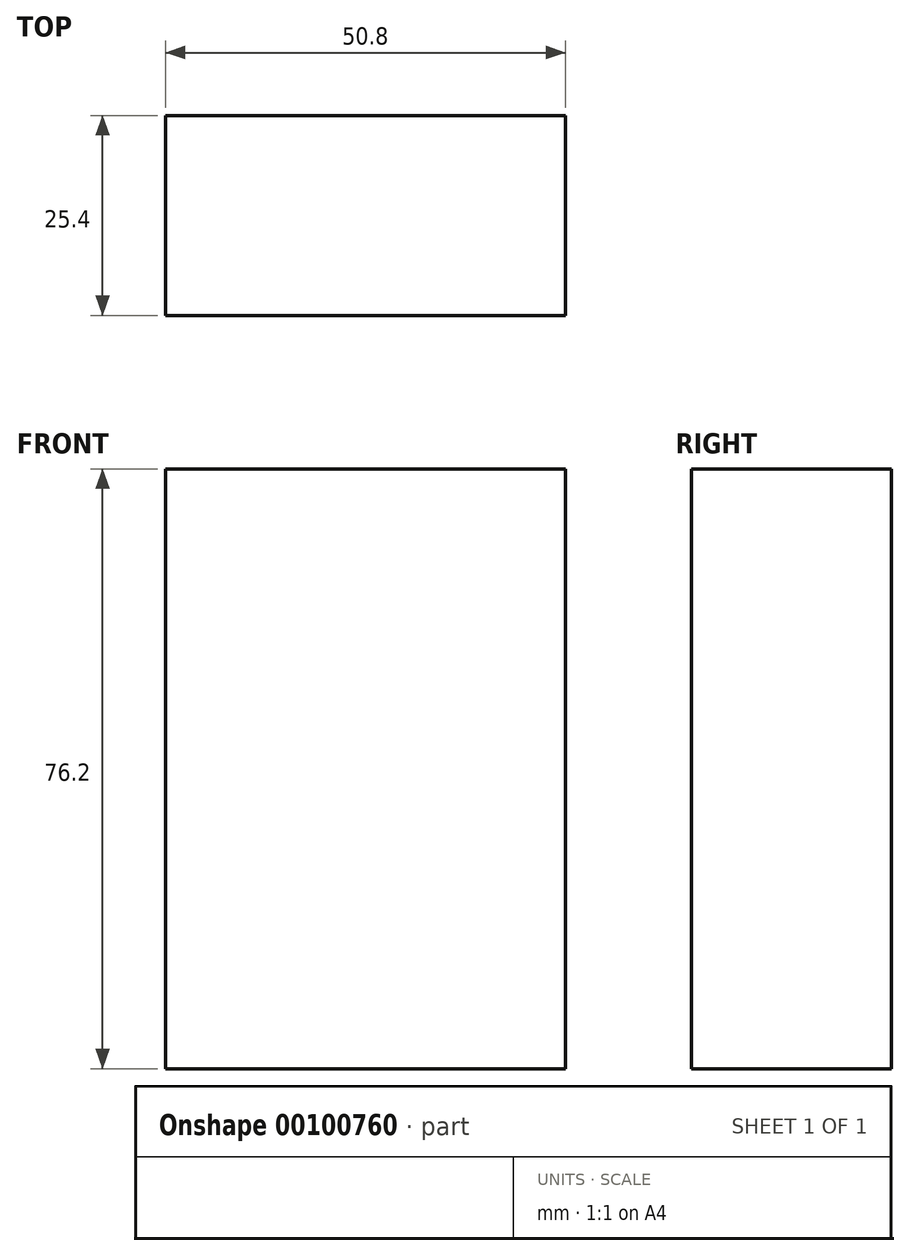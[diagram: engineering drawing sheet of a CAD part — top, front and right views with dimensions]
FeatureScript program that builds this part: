
annotation { "Feature Type Name" : "Feature", "Feature Type Description" : "" }
export const myFeature = defineFeature(function(context is Context, id is Id, definition is map)
    precondition{}
    {
        {
            var Q0;
            Q0=qCreatedBy(makeId("Front.planeOp"),FACE);
            var sketch = newSketch(context, id + "F0", { "sketchPlane" : qUnion([Q0])});
            skLineSegment(sketch, "E0.bottom", {"start": v(-25.4, 38.1) * mm, "end": v(25.4, 38.1) * mm});
            skLineSegment(sketch, "E0.top", {"start": v(-25.4, -38.1) * mm, "end": v(25.4, -38.1) * mm});
            skLineSegment(sketch, "E0.left", {"start": v(-25.4, 38.1) * mm, "end": v(-25.4, -38.1) * mm});
            skLineSegment(sketch, "E0.right", {"start": v(25.4, 38.1) * mm, "end": v(25.4, -38.1) * mm});
            skPoint(sketch, "E0.middle", {"position": v(0, 0) * mm});
            skSolve(sketch);
        }
        {
            var Q0;
            Q0=makeQuery(id+"F0.imprint","IMPRINT",FACE,{"disambiguationData":[TD([[makeQuery(id+"F0.imprint","IMPRINT",EDGE,{"derivedFrom":sQuery(id+"F0.wireOp",EDGE,"E0.bottom")}),-1.0]])]});
            extrude(context, id + "F1", {"entities" : qUnion([Q0]), "depth" : 25.4 * mm});
        }
        {
            var Q0;
            Q0 = qSketchRegion(id + "F0", true);
            extrude(context, id + "F2", {"entities" : qUnion([Q0]), "depth" : 25.4 * mm});
        }
    });
